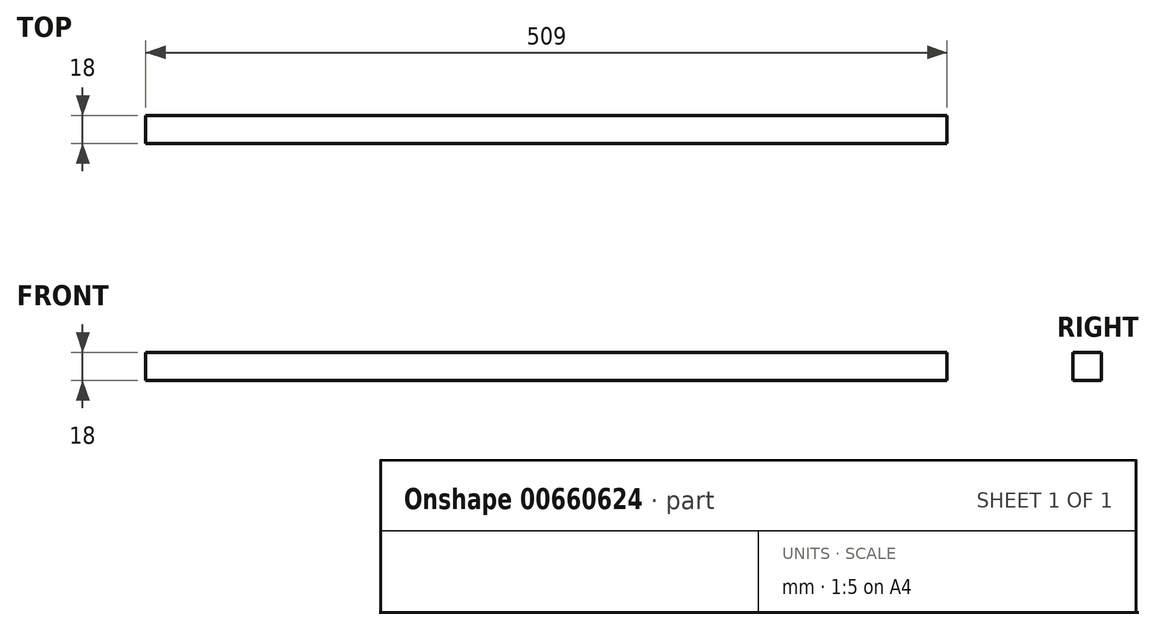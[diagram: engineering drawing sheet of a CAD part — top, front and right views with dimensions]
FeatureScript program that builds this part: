
annotation { "Feature Type Name" : "Feature", "Feature Type Description" : "" }
export const myFeature = defineFeature(function(context is Context, id is Id, definition is map)
    precondition{}
    {
        {
            var Q0;
            Q0=qCreatedBy(makeId("Front.planeOp"),FACE);
            var sketch = newSketch(context, id + "F0", { "sketchPlane" : qUnion([Q0])});
            skLineSegment(sketch, "E0.bottom", {"start": v(-253.47, 4.68) * mm, "end": v(255.53, 4.68) * mm});
            skLineSegment(sketch, "E0.top", {"start": v(-253.47, -13.32) * mm, "end": v(255.53, -13.32) * mm});
            skLineSegment(sketch, "E0.left", {"start": v(-253.47, 4.68) * mm, "end": v(-253.47, -13.32) * mm});
            skLineSegment(sketch, "E0.right", {"start": v(255.53, 4.68) * mm, "end": v(255.53, -13.32) * mm});
            skSolve(sketch);
        }
        {
            var Q0;
            Q0 = qSketchRegion(id + "F0", true);
            extrude(context, id + "F1", {"entities" : qUnion([Q0]), "depth" : 18 * mm, "offsetDistance" : 25 * mm});
        }
    });
